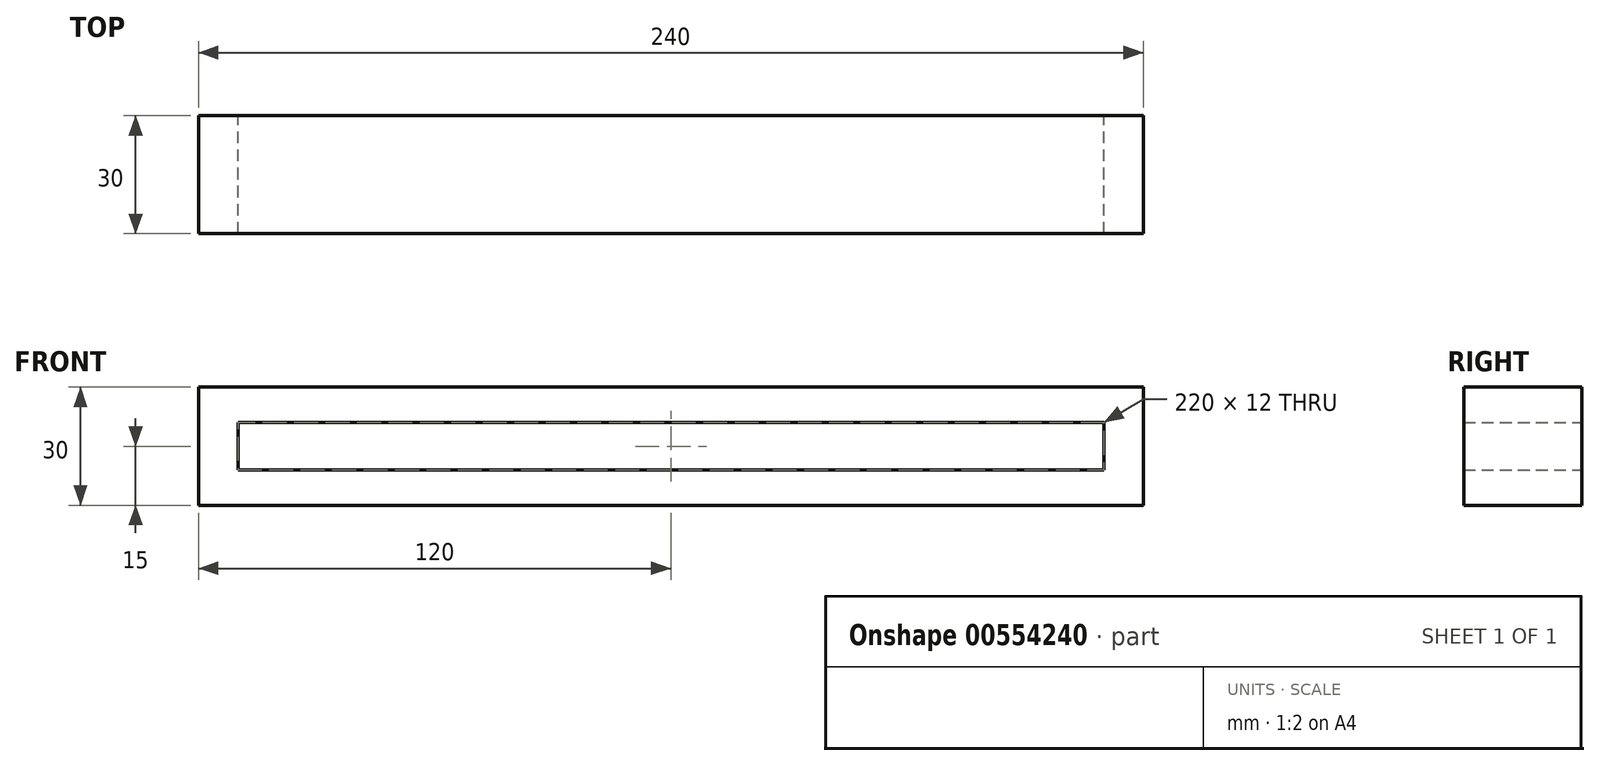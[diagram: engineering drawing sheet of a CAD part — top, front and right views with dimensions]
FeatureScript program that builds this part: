
annotation { "Feature Type Name" : "Feature", "Feature Type Description" : "" }
export const myFeature = defineFeature(function(context is Context, id is Id, definition is map)
    precondition{}
    {
        {
            var Q0;
            Q0=qCreatedBy(makeId("Front.planeOp"),FACE);
            var sketch = newSketch(context, id + "F0", { "sketchPlane" : qUnion([Q0])});
            skLineSegment(sketch, "E0.bottom", {"start": v(120, -15) * mm, "end": v(-120, -15) * mm});
            skLineSegment(sketch, "E0.top", {"start": v(120, 15) * mm, "end": v(-120, 15) * mm});
            skLineSegment(sketch, "E0.left", {"start": v(120, -15) * mm, "end": v(120, 15) * mm});
            skLineSegment(sketch, "E0.right", {"start": v(-120, -15) * mm, "end": v(-120, 15) * mm});
            skPoint(sketch, "E0.middle", {"position": v(0, 0) * mm});
            skLineSegment(sketch, "E1.bottom", {"start": v(110, -6) * mm, "end": v(-110, -6) * mm});
            skLineSegment(sketch, "E1.top", {"start": v(110, 6) * mm, "end": v(-110, 6) * mm});
            skLineSegment(sketch, "E1.left", {"start": v(110, -6) * mm, "end": v(110, 6) * mm});
            skLineSegment(sketch, "E1.right", {"start": v(-110, -6) * mm, "end": v(-110, 6) * mm});
            skSolve(sketch);
        }
        {
            var Q0;
            Q0=makeQuery(id+"F0.imprint","IMPRINT",FACE,{"disambiguationData":[TD([[makeQuery(id+"F0.imprint","IMPRINT",EDGE,{"derivedFrom":sQuery(id+"F0.wireOp",EDGE,"E0.bottom")}),-1.0]])]});
            extrude(context, id + "F1", {"entities" : qUnion([Q0]), "depth" : 30 * mm, "offsetDistance" : 25 * mm});
        }
    });
